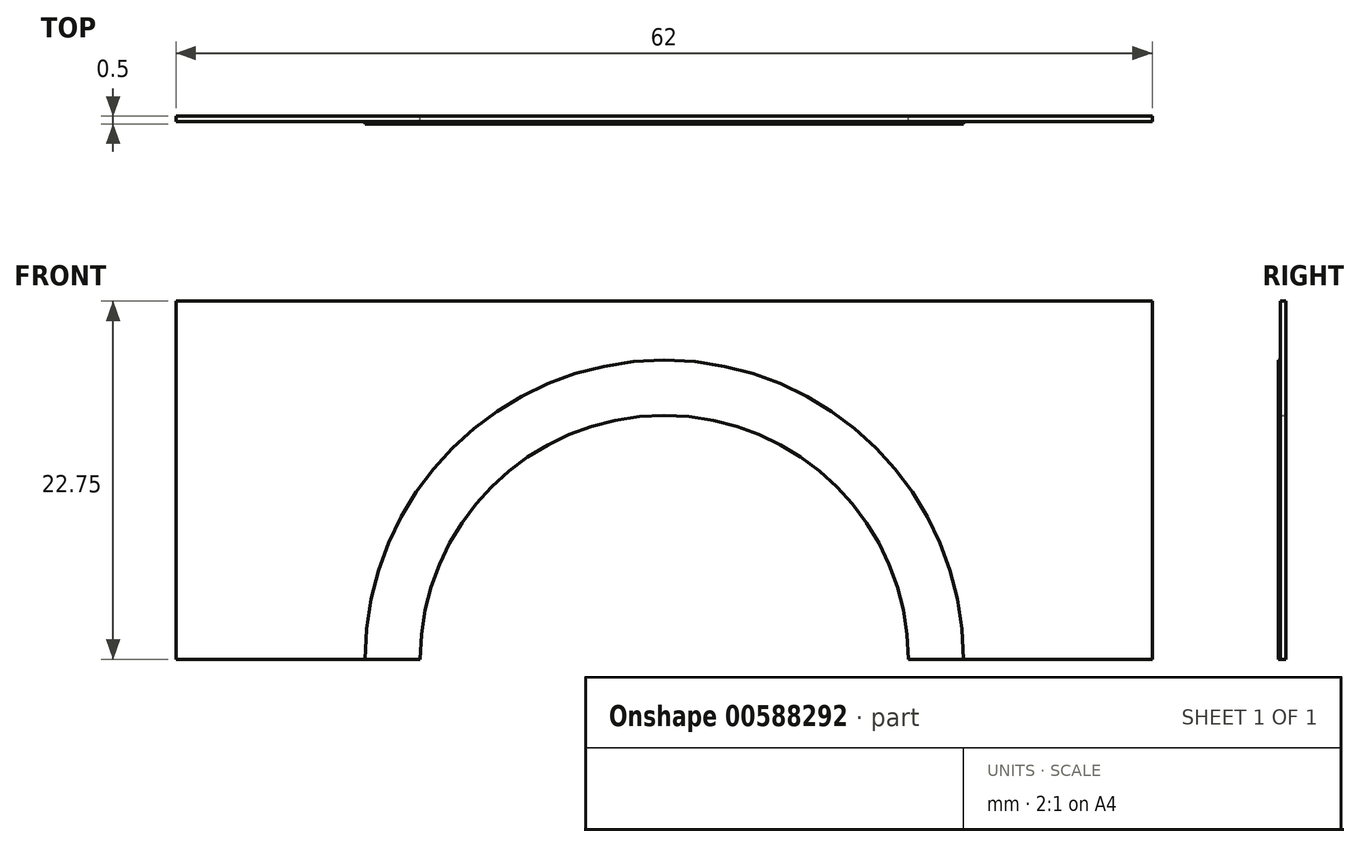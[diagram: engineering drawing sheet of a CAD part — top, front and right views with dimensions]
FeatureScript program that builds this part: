
annotation { "Feature Type Name" : "Feature", "Feature Type Description" : "" }
export const myFeature = defineFeature(function(context is Context, id is Id, definition is map)
    precondition{}
    {
        {
            var Q0;
            Q0=qCreatedBy(makeId("Front.planeOp"),FACE);
            var sketch = newSketch(context, id + "F0", { "sketchPlane" : qUnion([Q0])});
            skLineSegment(sketch, "E0", {"start": v(-190.52, -29.21) * mm, "end": v(-252.52, -29.21) * mm});
            skLineSegment(sketch, "E1", {"start": v(-252.52, -29.21) * mm, "end": v(-252.52, -51.96) * mm});
            skLineSegment(sketch, "E2", {"start": v(-252.52, -51.96) * mm, "end": v(-190.52, -51.96) * mm});
            skLineSegment(sketch, "E3", {"start": v(-190.52, -51.96) * mm, "end": v(-190.52, -29.21) * mm});
            skLineSegment(sketch, "E4", {"start": v(-252.52, -51.96) * mm, "end": v(-237.02, -51.96) * mm});
            skArc(sketch, "E5", {"start": v(-202.52, -51.96) * mm, "mid": v(-221.52, -32.96) * mm, "end": v(-240.52, -51.96) * mm});
            skArc(sketch, "E6", {"start": v(-206.02, -51.96) * mm, "mid": v(-221.52, -36.46) * mm, "end": v(-237.02, -51.96) * mm});
            skSolve(sketch);
        }
        {
            var Q0;
            Q0=makeQuery(id+"F0.imprint","IMPRINT",FACE,{"disambiguationData":[TD([[makeQuery(id+"F0.imprint","IMPRINT",EDGE,{"derivedFrom":sQuery(id+"F0.wireOp",EDGE,"E0")}),1.0]])]});
            extrude(context, id + "F1", {"entities" : qUnion([Q0]), "depth" : .35 * mm, "offsetDistance" : 25 * mm});
        }
        {
            var Q0;
            {var subQ0=sQuery(id+"F0.wireOp",EDGE,"E5");Q0=makeQuery(id+"F0.imprint","IMPRINT",FACE,{"disambiguationData":[TD([[makeQuery(id+"F0.imprint","IMPRINT",EDGE,{"derivedFrom":subQ0}),1.0]])]});}
            extrude(context, id + "F2", {"entities" : qUnion([Q0]), "operationType" : NewBodyOperationType.ADD, "depth" : .50 * mm, "offsetDistance" : 25 * mm});
        }
    });
